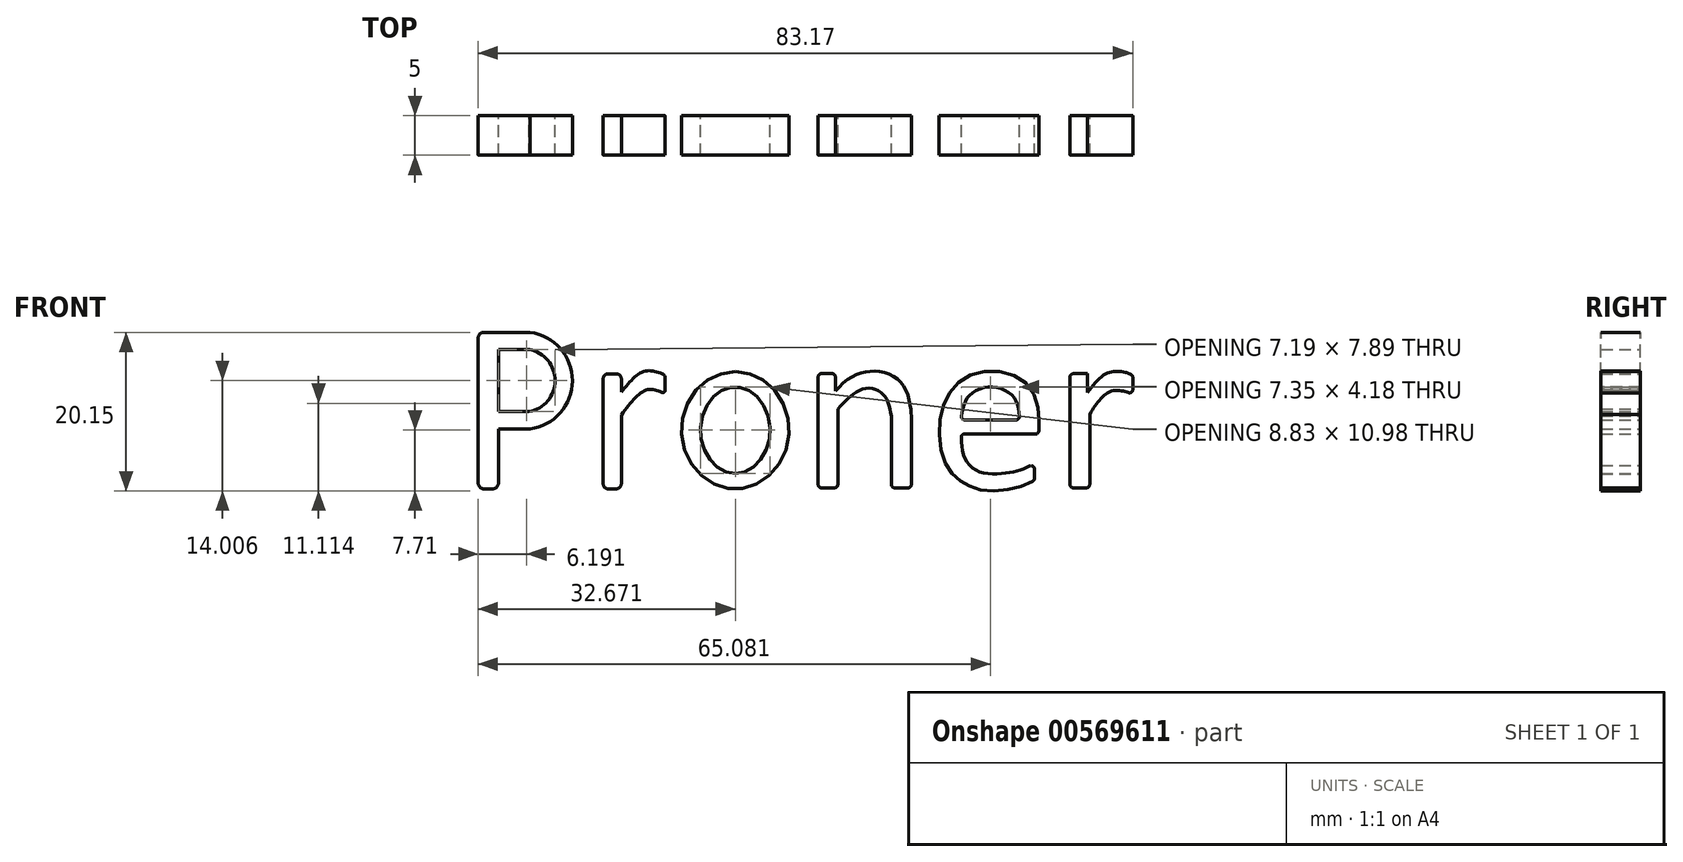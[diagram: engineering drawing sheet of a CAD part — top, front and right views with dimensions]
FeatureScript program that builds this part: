
annotation { "Feature Type Name" : "Feature", "Feature Type Description" : "" }
export const myFeature = defineFeature(function(context is Context, id is Id, definition is map)
    precondition{}
    {
        {
            var Q0;
            Q0=qCreatedBy(makeId("Front.planeOp"),FACE);
            var sketch = newSketch(context, id + "F0", { "sketchPlane" : qUnion([Q0])});
            skLineSegment(sketch, "E0", {"start": v(-61.38, -38.71) * mm, "end": v(-18.94, -38.71) * mm, "construction": true});
            skLineSegment(sketch, "E1.bottom", {"start": v(-56.6, -38.71) * mm, "end": v(-55.54, -38.71) * mm});
            skLineSegment(sketch, "E1.top", {"start": v(-56.6, -18.82) * mm, "end": v(-54.77, -18.82) * mm});
            skLineSegment(sketch, "E1.left", {"start": v(-57.37, -37.95) * mm, "end": v(-57.37, -19.58) * mm});
            skLineSegment(sketch, "E1.right", {"start": v(-54.77, -37.95) * mm, "end": v(-54.77, -31.1) * mm});
            skLineSegment(sketch, "E2", {"start": v(-54.77, -18.82) * mm, "end": v(-50.75, -18.82) * mm});
            skLineSegment(sketch, "E3", {"start": v(-54.77, -31.1) * mm, "end": v(-50.8, -31.1) * mm});
            skArc(sketch, "E4", {"start": v(-50.8, -31.1) * mm, "mid": v(-45.4, -24.98) * mm, "end": v(-50.75, -18.82) * mm});
            skLineSegment(sketch, "E5.0", {"start": v(-54.77, -28.9) * mm, "end": v(-50.89, -28.9) * mm});
            skArc(sketch, "E5.1", {"start": v(-50.89, -28.9) * mm, "mid": v(-47.59, -24.98) * mm, "end": v(-50.86, -21.02) * mm});
            skLineSegment(sketch, "E5.2", {"start": v(-54.77, -21.02) * mm, "end": v(-50.86, -21.02) * mm});
            skPoint(sketch, "E6.visualSharp", {"position": v(-57.37, -38.71) * mm});
            skArc(sketch, "E6.filletArc", {"start": v(-57.37, -37.95) * mm, "mid": v(-57.15, -38.49) * mm, "end": v(-56.6, -38.71) * mm});
            skPoint(sketch, "E7.visualSharp", {"position": v(-54.77, -38.71) * mm});
            skArc(sketch, "E7.filletArc", {"start": v(-55.54, -38.71) * mm, "mid": v(-55, -38.49) * mm, "end": v(-54.77, -37.95) * mm});
            skPoint(sketch, "E8.visualSharp", {"position": v(-57.37, -18.82) * mm});
            skArc(sketch, "E8.filletArc", {"start": v(-56.6, -18.82) * mm, "mid": v(-57.15, -19.04) * mm, "end": v(-57.37, -19.58) * mm});
            skLineSegment(sketch, "E9.trimOffspring", {"start": v(-54.77, -28.9) * mm, "end": v(-54.77, -21.02) * mm});
            skLineSegment(sketch, "E10.bottom", {"start": v(-40.83, -38.71) * mm, "end": v(-39.83, -38.71) * mm});
            skLineSegment(sketch, "E10.top", {"start": v(-40.83, -24.09) * mm, "end": v(-39.83, -24.09) * mm});
            skLineSegment(sketch, "E10.left", {"start": v(-41.49, -38.05) * mm, "end": v(-41.49, -24.75) * mm});
            skLineSegment(sketch, "E10.right", {"start": v(-39.17, -38.05) * mm, "end": v(-39.17, -29.3) * mm});
            skPoint(sketch, "E11.visualSharp", {"position": v(-41.49, -38.71) * mm});
            skArc(sketch, "E11.filletArc", {"start": v(-41.49, -38.05) * mm, "mid": v(-41.3, -38.52) * mm, "end": v(-40.83, -38.71) * mm});
            skPoint(sketch, "E12.visualSharp", {"position": v(-39.17, -38.71) * mm});
            skArc(sketch, "E12.filletArc", {"start": v(-39.83, -38.71) * mm, "mid": v(-39.36, -38.52) * mm, "end": v(-39.17, -38.05) * mm});
            skPoint(sketch, "E13.visualSharp", {"position": v(-39.17, -24.09) * mm});
            skArc(sketch, "E13.filletArc", {"start": v(-39.17, -24.75) * mm, "mid": v(-39.36, -24.28) * mm, "end": v(-39.83, -24.09) * mm});
            skPoint(sketch, "E14.visualSharp", {"position": v(-41.49, -24.09) * mm});
            skArc(sketch, "E14.filletArc", {"start": v(-40.83, -24.09) * mm, "mid": v(-41.3, -24.28) * mm, "end": v(-41.49, -24.75) * mm});
            skFitSpline(sketch, "E15", {"points": [v(-39.17, -26.4) * mm, v(-36.28, -23.8) * mm, v(-33.61, -24.22) * mm], "startDerivative": vector(5.14, 6.37) * mm, "endDerivative": vector(6.06, -2.26) * mm});
            skFitSpline(sketch, "E16", {"points": [v(-39.17, -29.3) * mm, v(-35.96, -26.14) * mm, v(-33.61, -26.65) * mm], "startDerivative": vector(5.55, 7.38) * mm, "endDerivative": vector(5.5, -2.62) * mm});
            skLineSegment(sketch, "E17", {"start": v(-33.61, -24.58) * mm, "end": v(-33.61, -26.19) * mm});
            skArc(sketch, "E18.filletArc", {"start": v(-34.03, -26.46) * mm, "mid": v(-33.75, -26.43) * mm, "end": v(-33.61, -26.19) * mm});
            skArc(sketch, "E19.filletArc", {"start": v(-33.61, -24.58) * mm, "mid": v(-33.7, -24.29) * mm, "end": v(-33.95, -24.1) * mm});
            skLineSegment(sketch, "E20.trimOffspring", {"start": v(-39.17, -26.4) * mm, "end": v(-39.17, -24.75) * mm});
            skLineSegment(sketch, "E21", {"start": v(-24.63, -39.74) * mm, "end": v(-24.63, -20) * mm, "construction": true});
            skLineSegment(sketch, "E22", {"start": v(-32.84, -31.26) * mm, "end": v(-16.55, -31.26) * mm, "construction": true});
            skEllipse(sketch, "E23", {"center": v(-24.7, -31.26) * mm, "majorRadius": 5.49 * mm, "minorRadius": 4.42 * mm, "majorAxis": v(0, -1)});
            skEllipse(sketch, "E24", {"center": v(-24.7, -31.26) * mm, "majorRadius": 6.83 * mm, "minorRadius": 7.44 * mm, "majorAxis": v(1, 0)});
            skLineSegment(sketch, "E25", {"start": v(-14.18, -38.17) * mm, "end": v(-14.18, -24.5) * mm});
            skLineSegment(sketch, "E26", {"start": v(-13.76, -24.08) * mm, "end": v(-12.4, -24.08) * mm});
            skLineSegment(sketch, "E27", {"start": v(-11.99, -24.5) * mm, "end": v(-11.99, -26.3) * mm});
            skFitSpline(sketch, "E28", {"points": [v(-11.99, -26.3) * mm, v(-10.27, -24.7) * mm, v(-8.5, -23.92) * mm, v(-6.87, -23.77) * mm, v(-5.1, -24.16) * mm, v(-3.66, -25.21) * mm, v(-2.8, -26.74) * mm, v(-2.41, -28.57) * mm, v(-2.33, -29.47) * mm], "startDerivative": vector(11.37, 12.13) * mm, "endDerivative": vector(0.56, -8.96) * mm});
            skLineSegment(sketch, "E29", {"start": v(-2.33, -29.47) * mm, "end": v(-2.33, -38.17) * mm});
            skLineSegment(sketch, "E30", {"start": v(-2.75, -38.58) * mm, "end": v(-4.46, -38.58) * mm});
            skLineSegment(sketch, "E31", {"start": v(-4.87, -38.17) * mm, "end": v(-4.87, -29.47) * mm});
            skFitSpline(sketch, "E32", {"points": [v(-4.87, -29.47) * mm, v(-5.42, -27.4) * mm, v(-6.55, -26.23) * mm, v(-8.24, -25.95) * mm, v(-10.07, -26.97) * mm, v(-11.67, -28.53) * mm], "startDerivative": vector(-1.8, 10.62) * mm, "endDerivative": vector(-7.16, -7.56) * mm});
            skLineSegment(sketch, "E33", {"start": v(-11.67, -28.53) * mm, "end": v(-11.67, -38.17) * mm});
            skLineSegment(sketch, "E34", {"start": v(-12.09, -38.58) * mm, "end": v(-13.76, -38.58) * mm});
            skPoint(sketch, "E35.visualSharp", {"position": v(-14.18, -24.08) * mm});
            skArc(sketch, "E35.filletArc", {"start": v(-13.76, -24.08) * mm, "mid": v(-14.05, -24.2) * mm, "end": v(-14.18, -24.5) * mm});
            skPoint(sketch, "E36.visualSharp", {"position": v(-11.99, -24.08) * mm});
            skArc(sketch, "E36.filletArc", {"start": v(-11.99, -24.5) * mm, "mid": v(-12.1, -24.2) * mm, "end": v(-12.4, -24.08) * mm});
            skPoint(sketch, "E37.visualSharp", {"position": v(-2.33, -38.58) * mm});
            skArc(sketch, "E37.filletArc", {"start": v(-2.75, -38.58) * mm, "mid": v(-2.45, -38.46) * mm, "end": v(-2.33, -38.17) * mm});
            skPoint(sketch, "E38.visualSharp", {"position": v(-4.87, -38.58) * mm});
            skArc(sketch, "E38.filletArc", {"start": v(-4.87, -38.17) * mm, "mid": v(-4.75, -38.46) * mm, "end": v(-4.46, -38.58) * mm});
            skPoint(sketch, "E39.visualSharp", {"position": v(-11.67, -38.58) * mm});
            skArc(sketch, "E39.filletArc", {"start": v(-12.09, -38.58) * mm, "mid": v(-11.8, -38.46) * mm, "end": v(-11.67, -38.17) * mm});
            skPoint(sketch, "E40.visualSharp", {"position": v(-14.18, -38.58) * mm});
            skArc(sketch, "E40.filletArc", {"start": v(-14.18, -38.17) * mm, "mid": v(-14.05, -38.46) * mm, "end": v(-13.76, -38.58) * mm});
            skLineSegment(sketch, "E41", {"start": v(4.42, -31.75) * mm, "end": v(13.45, -31.75) * mm});
            skFitSpline(sketch, "E42", {"points": [v(13.84, -31.75) * mm, v(13.84, -29.17) * mm, v(12.62, -25.69) * mm, v(8.8, -23.77) * mm, v(4.57, -24.55) * mm, v(2, -27.49) * mm, v(1.21, -31.75) * mm, v(2.23, -35.93) * mm, v(4.03, -37.76) * mm, v(6.22, -38.78) * mm, v(10.12, -38.78) * mm, v(13.29, -37.69) * mm], "startDerivative": vector(1.72, 31.5) * mm, "endDerivative": vector(33.74, 14.72) * mm});
            skLineSegment(sketch, "E43", {"start": v(13.29, -37.42) * mm, "end": v(13.29, -36.18) * mm});
            skFitSpline(sketch, "E44", {"points": [v(13.29, -35.5) * mm, v(11.65, -36.28) * mm, v(9.38, -36.75) * mm, v(6.25, -36.51) * mm, v(4.46, -34.8) * mm, v(3.99, -31.75) * mm], "startDerivative": vector(-9.36, -5.06) * mm, "endDerivative": vector(-0.57, 14.8) * mm});
            skArc(sketch, "E45.filletArc", {"start": v(13.29, -36.18) * mm, "mid": v(13.1, -35.83) * mm, "end": v(12.69, -35.82) * mm});
            skArc(sketch, "E46.filletArc", {"start": v(13.04, -37.8) * mm, "mid": v(13.22, -37.64) * mm, "end": v(13.29, -37.42) * mm});
            skArc(sketch, "E47.filletArc", {"start": v(4.42, -31.75) * mm, "mid": v(4.12, -31.87) * mm, "end": v(4, -32.18) * mm});
            skArc(sketch, "E48.filletArc", {"start": v(13.45, -31.75) * mm, "mid": v(13.73, -31.63) * mm, "end": v(13.86, -31.35) * mm});
            skLineSegment(sketch, "E49", {"start": v(4.45, -29.95) * mm, "end": v(10.97, -29.95) * mm});
            skFitSpline(sketch, "E50", {"points": [v(11.41, -29.95) * mm, v(10.67, -27.06) * mm, v(7.58, -25.77) * mm, v(4.77, -27.17) * mm, v(3.99, -29.95) * mm], "startDerivative": vector(-0.8, 12.9) * mm, "endDerivative": vector(-1.37, -12.43) * mm});
            skArc(sketch, "E51.filletArc", {"start": v(4.04, -29.49) * mm, "mid": v(4.14, -29.8) * mm, "end": v(4.45, -29.95) * mm});
            skArc(sketch, "E52.filletArc", {"start": v(10.97, -29.95) * mm, "mid": v(11.28, -29.82) * mm, "end": v(11.38, -29.5) * mm});
            skLineSegment(sketch, "E53", {"start": v(17.82, -38.17) * mm, "end": v(17.82, -24.5) * mm});
            skLineSegment(sketch, "E54", {"start": v(18.23, -24.09) * mm, "end": v(20.05, -24.09) * mm});
            skLineSegment(sketch, "E55", {"start": v(20.05, -24.09) * mm, "end": v(20.05, -26.47) * mm});
            skFitSpline(sketch, "E56", {"points": [v(20.05, -26.47) * mm, v(22.16, -24.2) * mm, v(23.76, -23.77) * mm, v(25.1, -23.97) * mm, v(25.8, -24.32) * mm], "startDerivative": vector(6.04, 7.86) * mm, "endDerivative": vector(3.65, -2.2) * mm});
            skLineSegment(sketch, "E57", {"start": v(25.8, -24.55) * mm, "end": v(25.8, -26.1) * mm});
            skFitSpline(sketch, "E58", {"points": [v(25.8, -26.7) * mm, v(24.66, -26.31) * mm, v(23.14, -26.27) * mm, v(21.65, -27.33) * mm, v(20.32, -29.24) * mm], "startDerivative": vector(-5.1, 2.05) * mm, "endDerivative": vector(-4.27, -6.93) * mm});
            skLineSegment(sketch, "E59", {"start": v(20.32, -29.24) * mm, "end": v(20.32, -38.17) * mm});
            skLineSegment(sketch, "E60", {"start": v(19.91, -38.58) * mm, "end": v(18.23, -38.58) * mm});
            skPoint(sketch, "E61.visualSharp", {"position": v(17.82, -38.58) * mm});
            skArc(sketch, "E61.filletArc", {"start": v(17.82, -38.17) * mm, "mid": v(17.94, -38.46) * mm, "end": v(18.23, -38.58) * mm});
            skPoint(sketch, "E62.visualSharp", {"position": v(20.32, -38.58) * mm});
            skArc(sketch, "E62.filletArc", {"start": v(19.91, -38.58) * mm, "mid": v(20.2, -38.46) * mm, "end": v(20.32, -38.17) * mm});
            skPoint(sketch, "E63.visualSharp", {"position": v(17.82, -24.09) * mm});
            skArc(sketch, "E63.filletArc", {"start": v(18.23, -24.09) * mm, "mid": v(17.94, -24.2) * mm, "end": v(17.82, -24.5) * mm});
            skArc(sketch, "E64.filletArc", {"start": v(25.8, -24.55) * mm, "mid": v(25.74, -24.35) * mm, "end": v(25.59, -24.2) * mm});
            skArc(sketch, "E65.filletArc", {"start": v(25.24, -26.5) * mm, "mid": v(25.62, -26.44) * mm, "end": v(25.8, -26.1) * mm});
            skSolve(sketch);
        }
        {
            var Q0;
            Q0 = qSketchRegion(id + "F0", true);
            extrude(context, id + "F1", {"entities" : qUnion([Q0]), "depth" : 5 * mm, "offsetDistance" : 25 * mm});
        }
    });
